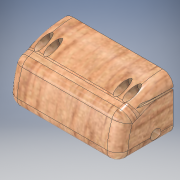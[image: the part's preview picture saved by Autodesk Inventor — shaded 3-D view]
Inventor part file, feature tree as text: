
AUTODESK INVENTOR PART (.ipt)
format: ipt  version: 2017 (Build 210142000, 142)  size: 319,488 bytes
history: native  units: in
note: dims shown in document units (in); Inventor stores cm internally (conversion verified against a paired STEP export)
features: sketch x7, extrude x4, hole x3, fillet x2, plane x1, projected_geometry x1
ambient origin geometry x8: Origin, YZ Plane, XZ Plane, XY Plane, X Axis, Y Axis, Z Axis, Center Point
bodies: Solid1 (feature_tree)
feature tree (18):
  extrude  "Extrusion1"  Depth=1.53in
  fillet  "Fillet5"  Radius=1.6in
  extrude  "Extrusion2"  Depth=1.4in
  fillet  "Fillet6"  Radius=1.1in
  plane  "Work Plane1"
  hole  "Hole1"  [1 undecoded]
  hole  "Hole2"  [1 undecoded]
  hole  "Hole3"  [1 undecoded]
  extrude  "Extrusion3"  Depth=1.6in
  extrude  "Extrusion4"  Depth=0.06in
  sketch  "Sketch1"  dims[d0=3.17in d1=1.53in d2=1.6in d3=0.0in]
  sketch  "Sketch5"  dims[d11=0.3in d12=1.4in d13=1.1in]
  sketch  "Sketch6"  dims[d14=1.25in d15=1.15in]
  sketch  "Sketch7"  dims[d16=0.2in d17=0.3in]
  sketch  "Sketch8"  dims[d18=2.3007in d19=3.7in d20=0.0in]
  sketch  "Sketch9"  dims[d21=0.3in d22=1.6in]
  projected_geometry  "Projected Loop1"
  sketch  "Sketch10"  dims[d23=0.32in d24=0.27in d25=0.18in d26=0.18in d27=0.32in d28=0.27in d29=0.18in d30=0.18in d31=0.2in d32=0.75in d33=0.375in d34=0.25in d35=0.5635in d36=1.0in d37=0.8108in d40=0.3in d41=0.5in d42=0.29in d43=0.75in d44=0.375in d45=0.25in d46=0.5635in d47=0.35in d48=0.8108in d49=0.29in d50=0.75in d51=0.375in d52=0.25in d53=0.5635in d54=0.35in d55=0.8108in d56=0.39in d57=0.39in d58=0.3in d59=0.3in d60=0.2in d61=0.57in d62=0.0in d63=0.3in d64=0.06in d65=0.06in d66=0.3in d67=0.06in d69=0.06in d70=0.57in d71=0.0in]
note: 3 required parameter values undecoded (feature->parameter linkage not recoverable at this tier; creation-order binding heuristic only, values carry confidence <= 0.55)
